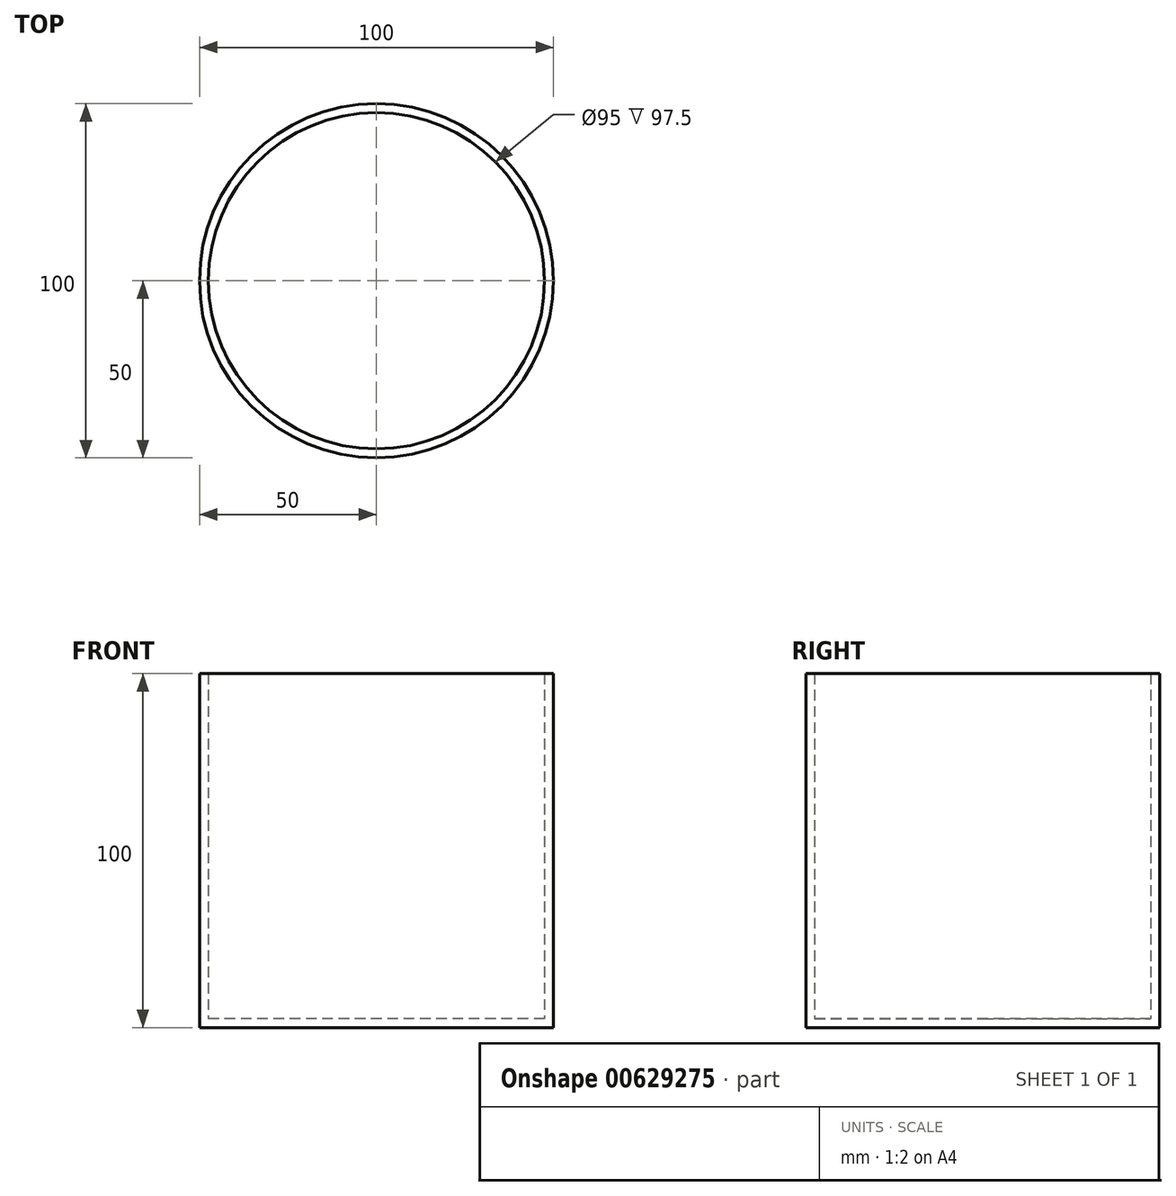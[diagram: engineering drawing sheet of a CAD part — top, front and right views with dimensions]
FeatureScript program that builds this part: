
annotation { "Feature Type Name" : "Feature", "Feature Type Description" : "" }
export const myFeature = defineFeature(function(context is Context, id is Id, definition is map)
    precondition{}
    {
        {
            var Q0;
            Q0=qCreatedBy(makeId("Top.planeOp"),FACE);
            var sketch = newSketch(context, id + "F0", { "sketchPlane" : qUnion([Q0])});
            skCircle(sketch, "E0", {"center": v(0, 0) * mm, "radius": 50 * mm});
            skSolve(sketch);
        }
        {
            var Q0;
            Q0=makeQuery(id+"F0.imprint","IMPRINT",FACE,{"disambiguationData":[TD([[makeQuery(id+"F0.imprint","IMPRINT",EDGE,{"derivedFrom":sQuery(id+"F0.wireOp",EDGE,"E0")}),1.0]])]});
            extrude(context, id + "F1", {"entities" : qUnion([Q0]), "depth" : 100 * mm, "offsetDistance" : 25 * mm});
        }
        {
            var Q0;
            Q0=makeQuery(id+"F1.opExtrude","CAP_FACE",FACE,{"disambiguationData":[OSD([sQuery(id+"F0.wireOp",EDGE,"E0")])],"isStart":false});
            shell(context, id + "F2", {"entities" : qUnion([Q0]), "thickness" : 2.5 * mm});
        }
        {
            var Q0;
            Q0=qCreatedBy(makeId("Front.planeOp"),FACE);
            cPlane(context, id + "F3", {"entities" : qUnion([Q0]), "cplaneType" : CPlaneType.OFFSET, "offset" : 50 * mm, "width" : 150 * mm, "height" : 150 * mm});
        }
        {
            var Q0;
            Q0=qCreatedBy(id+"F3.planeOp",FACE);
            var sketch = newSketch(context, id + "F4", { "sketchPlane" : qUnion([Q0])});
            skCircle(sketch, "E1", {"center": v(0, 94.44) * mm, "radius": 5 * mm});
            skCircle(sketch, "E2", {"center": v(0, 7.78) * mm, "radius": 5 * mm});
            skSolve(sketch);
        }
        {
            var Q0;
            Q0=qCreatedBy(makeId("Right.planeOp"),FACE);
            var sketch = newSketch(context, id + "F5", { "sketchPlane" : qUnion([Q0])});
            skFitSpline(sketch, "E3", {"points": [v(-49.83, 95.46) * mm, v(-70.3, 98.75) * mm, v(-71.04, 19.05) * mm, v(-49.83, 7.72) * mm], "startDerivative": vector(-93.06, 54.26) * mm, "endDerivative": vector(90.25, -6.7) * mm});
            skSolve(sketch);
        }
    });
